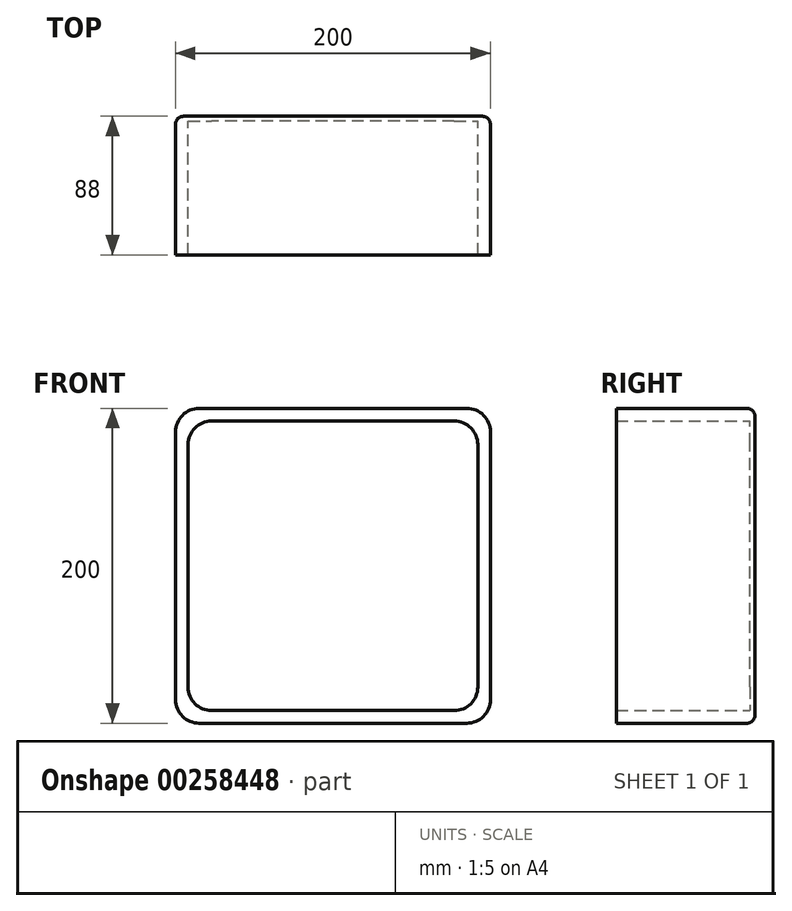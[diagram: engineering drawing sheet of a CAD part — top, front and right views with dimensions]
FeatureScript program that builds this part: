
annotation { "Feature Type Name" : "Feature", "Feature Type Description" : "" }
export const myFeature = defineFeature(function(context is Context, id is Id, definition is map)
    precondition{}
    {
        {
            var Q0;
            Q0=qCreatedBy(makeId("Front.planeOp"),FACE);
            var sketch = newSketch(context, id + "F0", { "sketchPlane" : qUnion([Q0])});
            skLineSegment(sketch, "E0.rect.bottom", {"start": v(100, -100) * mm, "end": v(-100, -100) * mm});
            skLineSegment(sketch, "E0.rect.top", {"start": v(100, 100) * mm, "end": v(-100, 100) * mm});
            skLineSegment(sketch, "E0.rect.left", {"start": v(100, -100) * mm, "end": v(100, 100) * mm});
            skLineSegment(sketch, "E0.rect.right", {"start": v(-100, -100) * mm, "end": v(-100, 100) * mm});
            skPoint(sketch, "E0.rect.middle", {"position": v(0, 0) * mm});
            skLineSegment(sketch, "E1.rect.bottom", {"start": v(92, -92) * mm, "end": v(-92, -92) * mm});
            skLineSegment(sketch, "E1.rect.top", {"start": v(92, 92) * mm, "end": v(-92, 92) * mm});
            skLineSegment(sketch, "E1.rect.left", {"start": v(92, -92) * mm, "end": v(92, 92) * mm});
            skLineSegment(sketch, "E1.rect.right", {"start": v(-92, -92) * mm, "end": v(-92, 92) * mm});
            skSolve(sketch);
        }
        {
            var Q0;
            Q0=makeQuery(id+"F0.imprint","IMPRINT",FACE,{"disambiguationData":[TD([[makeQuery(id+"F0.imprint","IMPRINT",EDGE,{"derivedFrom":sQuery(id+"F0.wireOp",EDGE,"E0.rect.bottom")}),-1.0]])]});
            extrude(context, id + "F1", {"entities" : qUnion([Q0]), "depth" : 85 * mm});
        }
        {
            var Q0;
            Q0=makeQuery(id+"F1.opExtrude","SWEPT_EDGE",EDGE,{"disambiguationData":[OSD([sQuery(id+"F0.wireOp",EDGE,"E0.rect.top"),sQuery(id+"F0.wireOp",EDGE,"E0.rect.right")])]});
            var Q1;
            Q1=makeQuery(id+"F1.opExtrude","SWEPT_EDGE",EDGE,{"disambiguationData":[OSD([sQuery(id+"F0.wireOp",EDGE,"E1.rect.top"),sQuery(id+"F0.wireOp",EDGE,"E1.rect.right")])]});
            var Q2;
            Q2=makeQuery(id+"F1.opExtrude","SWEPT_EDGE",EDGE,{"disambiguationData":[OSD([sQuery(id+"F0.wireOp",EDGE,"E0.rect.top"),sQuery(id+"F0.wireOp",EDGE,"E0.rect.left")])]});
            var Q3;
            Q3=makeQuery(id+"F1.opExtrude","SWEPT_EDGE",EDGE,{"disambiguationData":[OSD([sQuery(id+"F0.wireOp",EDGE,"E1.rect.top"),sQuery(id+"F0.wireOp",EDGE,"E1.rect.left")])]});
            var Q4;
            Q4=makeQuery(id+"F1.opExtrude","SWEPT_EDGE",EDGE,{"disambiguationData":[OSD([sQuery(id+"F0.wireOp",EDGE,"E0.rect.bottom"),sQuery(id+"F0.wireOp",EDGE,"E0.rect.left")])]});
            var Q5;
            Q5=makeQuery(id+"F1.opExtrude","SWEPT_EDGE",EDGE,{"disambiguationData":[OSD([sQuery(id+"F0.wireOp",EDGE,"E1.rect.bottom"),sQuery(id+"F0.wireOp",EDGE,"E1.rect.left")])]});
            var Q6;
            Q6=makeQuery(id+"F1.opExtrude","SWEPT_EDGE",EDGE,{"disambiguationData":[OSD([sQuery(id+"F0.wireOp",EDGE,"E1.rect.bottom"),sQuery(id+"F0.wireOp",EDGE,"E1.rect.right")])]});
            var Q7;
            Q7=makeQuery(id+"F1.opExtrude","SWEPT_EDGE",EDGE,{"disambiguationData":[OSD([sQuery(id+"F0.wireOp",EDGE,"E0.rect.bottom"),sQuery(id+"F0.wireOp",EDGE,"E0.rect.right")])]});
            fillet(context, id + "F2", {"entities" : qUnion([Q0, Q1, Q2, Q3, Q4, Q5, Q6, Q7]), "radius" : 15 * mm, "tangentPropagation" : true, "allowEdgeOverflow" : false});
        }
        {
            var Q0;
            Q0=makeQuery(id+"F1.opExtrude","CAP_FACE",FACE,{"disambiguationData":[OSD([sQuery(id+"F0.wireOp",EDGE,"E0.rect.bottom"),sQuery(id+"F0.wireOp",EDGE,"E0.rect.top"),sQuery(id+"F0.wireOp",EDGE,"E0.rect.left"),sQuery(id+"F0.wireOp",EDGE,"E0.rect.right"),sQuery(id+"F0.wireOp",EDGE,"E1.rect.bottom"),sQuery(id+"F0.wireOp",EDGE,"E1.rect.top"),sQuery(id+"F0.wireOp",EDGE,"E1.rect.left"),sQuery(id+"F0.wireOp",EDGE,"E1.rect.right")])],"isStart":true});
            var sketch = newSketch(context, id + "F3", { "sketchPlane" : qUnion([Q0])});
            skLineSegment(sketch, "E2.rect.bottom", {"start": v(85, -100) * mm, "end": v(-85, -100) * mm});
            skLineSegment(sketch, "E2.rect.top", {"start": v(85, 100) * mm, "end": v(-85, 100) * mm});
            skLineSegment(sketch, "E2.rect.left", {"start": v(100, -85) * mm, "end": v(100, 85) * mm});
            skLineSegment(sketch, "E2.rect.right", {"start": v(-100, -85) * mm, "end": v(-100, 85) * mm});
            skPoint(sketch, "E2.rect.middle", {"position": v(0, 0) * mm});
            skPoint(sketch, "E3.visualSharp", {"position": v(-100, 100) * mm});
            skArc(sketch, "E3.filletArc", {"start": v(-85, 100) * mm, "mid": v(-95.6, 95.6) * mm, "end": v(-100, 85) * mm});
            skPoint(sketch, "E4.visualSharp", {"position": v(100, 100) * mm});
            skArc(sketch, "E4.filletArc", {"start": v(100, 85) * mm, "mid": v(95.6, 95.6) * mm, "end": v(85, 100) * mm});
            skPoint(sketch, "E5.visualSharp", {"position": v(100, -100) * mm});
            skArc(sketch, "E5.filletArc", {"start": v(85, -100) * mm, "mid": v(95.6, -95.6) * mm, "end": v(100, -85) * mm});
            skPoint(sketch, "E6.visualSharp", {"position": v(-100, -100) * mm});
            skArc(sketch, "E6.filletArc", {"start": v(-100, -85) * mm, "mid": v(-95.6, -95.6) * mm, "end": v(-85, -100) * mm});
            skSolve(sketch);
        }
        {
            var Q0;
            Q0=qSketchRegion(id+"F3",true);
            extrude(context, id + "F4", {"entities" : qUnion([Q0]), "operationType" : NewBodyOperationType.ADD, "depth" : 3 * mm});
        }
        {
            var Q0;
            Q0=makeQuery(id+"F4.opExtrude","CAP_EDGE",EDGE,{"disambiguationData":[OSD([sQuery(id+"F3.wireOp",EDGE,"E6.filletArc")])],"isStart":false});
            fillet(context, id + "F5", {"entities" : qUnion([Q0]), "radius" : 5 * mm, "tangentPropagation" : true, "allowEdgeOverflow" : false});
        }
    });
